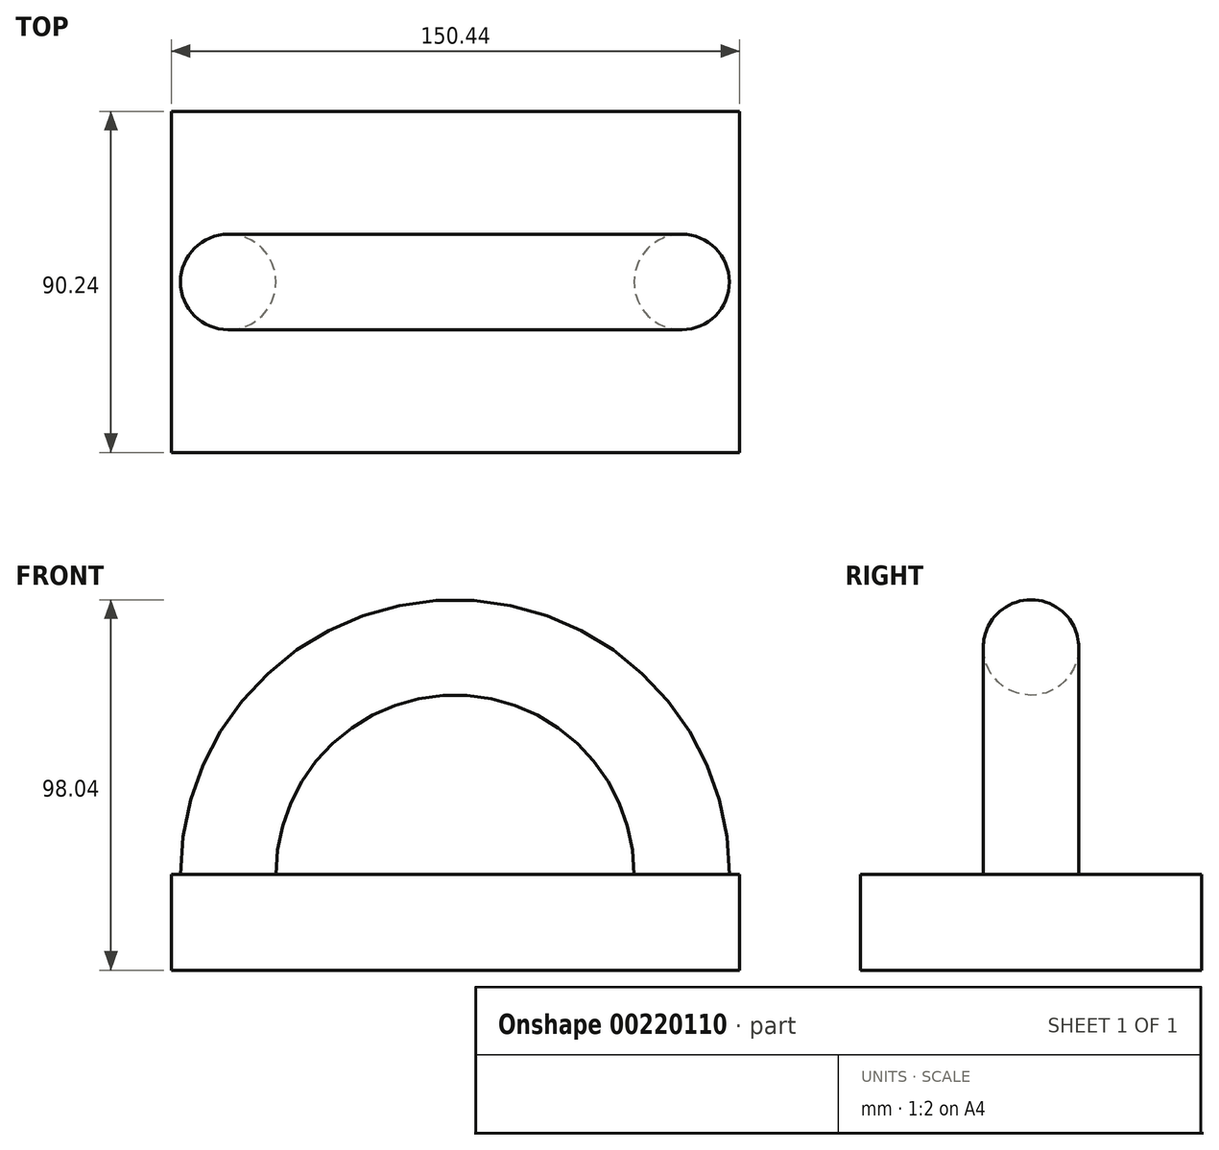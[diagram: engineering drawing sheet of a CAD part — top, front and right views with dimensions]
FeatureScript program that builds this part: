
annotation { "Feature Type Name" : "Feature", "Feature Type Description" : "" }
export const myFeature = defineFeature(function(context is Context, id is Id, definition is map)
    precondition{}
    {
        {
            var Q0;
            Q0=qCreatedBy(makeId("Top.planeOp"),FACE);
            var sketch = newSketch(context, id + "F0", { "sketchPlane" : qUnion([Q0])});
            skLineSegment(sketch, "E0.bottom", {"start": v(0, 45.12) * mm, "end": v(75.35, 45.12) * mm});
            skLineSegment(sketch, "E0.top", {"start": v(0, -45.12) * mm, "end": v(75.35, -45.12) * mm});
            skLineSegment(sketch, "E0.left", {"start": v(0, 45.12) * mm, "end": v(0, -45.12) * mm});
            skLineSegment(sketch, "E0.right", {"start": v(75.35, 45.12) * mm, "end": v(75.35, -45.12) * mm});
            skPoint(sketch, "E0.middle", {"position": v(37.68, 0) * mm});
            skLineSegment(sketch, "E1.bottom", {"start": v(-75.09, 45.12) * mm, "end": v(0, 45.12) * mm});
            skLineSegment(sketch, "E1.top", {"start": v(-75.09, -45.12) * mm, "end": v(0, -45.12) * mm});
            skLineSegment(sketch, "E1.left", {"start": v(-75.09, 45.12) * mm, "end": v(-75.09, -45.12) * mm});
            skPoint(sketch, "E1.middle", {"position": v(-37.54, 0) * mm});
            skPoint(sketch, "E2.end.orphan", {"position": v(-75.09, 0) * mm});
            skPoint(sketch, "E3.orphan", {"position": v(0, 0) * mm});
            skPoint(sketch, "E4.end.orphan", {"position": v(75.35, 0) * mm});
            skSolve(sketch);
        }
        {
            var Q0;
            Q0=makeQuery(id+"F0.imprint","IMPRINT",FACE,{"disambiguationData":[TD([[makeQuery(id+"F0.imprint","IMPRINT",EDGE,{"derivedFrom":sQuery(id+"F0.wireOp",EDGE,"E0.bottom")}),-1.0]])]});
            var sketch = newSketch(context, id + "F1", { "sketchPlane" : qUnion([Q0])});
            skCircle(sketch, "E5", {"center": v(60.01, 0) * mm, "radius": 12.63 * mm});
            skLineSegment(sketch, "E6", {"start": v(0, -42.59) * mm, "end": v(0, 44.34) * mm});
            skSolve(sketch);
        }
        {
            var Q0;
            Q0 = qSketchRegion(id + "F0", true);
            extrude(context, id + "F2", {"entities" : qUnion([Q0]), "oppositeDirection" : true, "depth" : 25.4 * mm});
        }
        {
            var Q0;
            Q0=makeQuery(id+"F1.imprint","IMPRINT",FACE,{"disambiguationData":[TD([[makeQuery(id+"F1.imprint","IMPRINT",EDGE,{"derivedFrom":sQuery(id+"F1.wireOp",EDGE,"E5")}),1.0]])]});
            var Q1;
            Q1=sQuery(id+"F1.wireOp",EDGE,"E6");
            revolve(context, id + "F3", {"operationType" : NewBodyOperationType.ADD, "entities" : qUnion([Q0]), "axis" : qUnion([Q1]), "revolveType" : RevolveType.ONE_DIRECTION, "oppositeDirection" : true, "angle" : 180 * degree});
        }
    });
